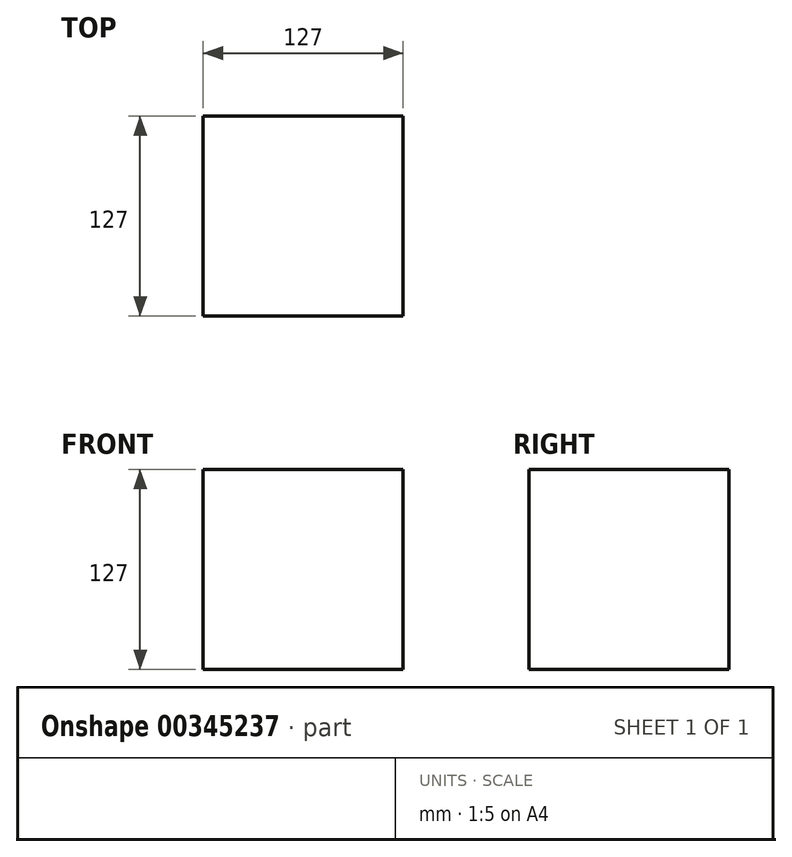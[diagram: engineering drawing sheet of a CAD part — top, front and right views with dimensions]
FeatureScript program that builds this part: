
annotation { "Feature Type Name" : "Feature", "Feature Type Description" : "" }
export const myFeature = defineFeature(function(context is Context, id is Id, definition is map)
    precondition{}
    {
        {
            var Q0;
            Q0=qCreatedBy(makeId("Front.planeOp"),FACE);
            var sketch = newSketch(context, id + "F0", { "sketchPlane" : qUnion([Q0])});
            skLineSegment(sketch, "E0.bottom", {"start": v(-80.82, 70.66) * mm, "end": v(46.18, 70.66) * mm});
            skLineSegment(sketch, "E0.top", {"start": v(-80.82, -56.34) * mm, "end": v(46.18, -56.34) * mm});
            skLineSegment(sketch, "E0.left", {"start": v(-80.82, 70.66) * mm, "end": v(-80.82, -56.34) * mm});
            skLineSegment(sketch, "E0.right", {"start": v(46.18, 70.66) * mm, "end": v(46.18, -56.34) * mm});
            skSolve(sketch);
        }
        {
            var Q0;
            Q0=makeQuery(id+"F0.imprint","IMPRINT",FACE,{"disambiguationData":[TD([[makeQuery(id+"F0.imprint","IMPRINT",EDGE,{"derivedFrom":sQuery(id+"F0.wireOp",EDGE,"E0.bottom")}),-1.0]])]});
            extrude(context, id + "F1", {"entities" : qUnion([Q0]), "depth" : 127 * mm});
        }
    });
